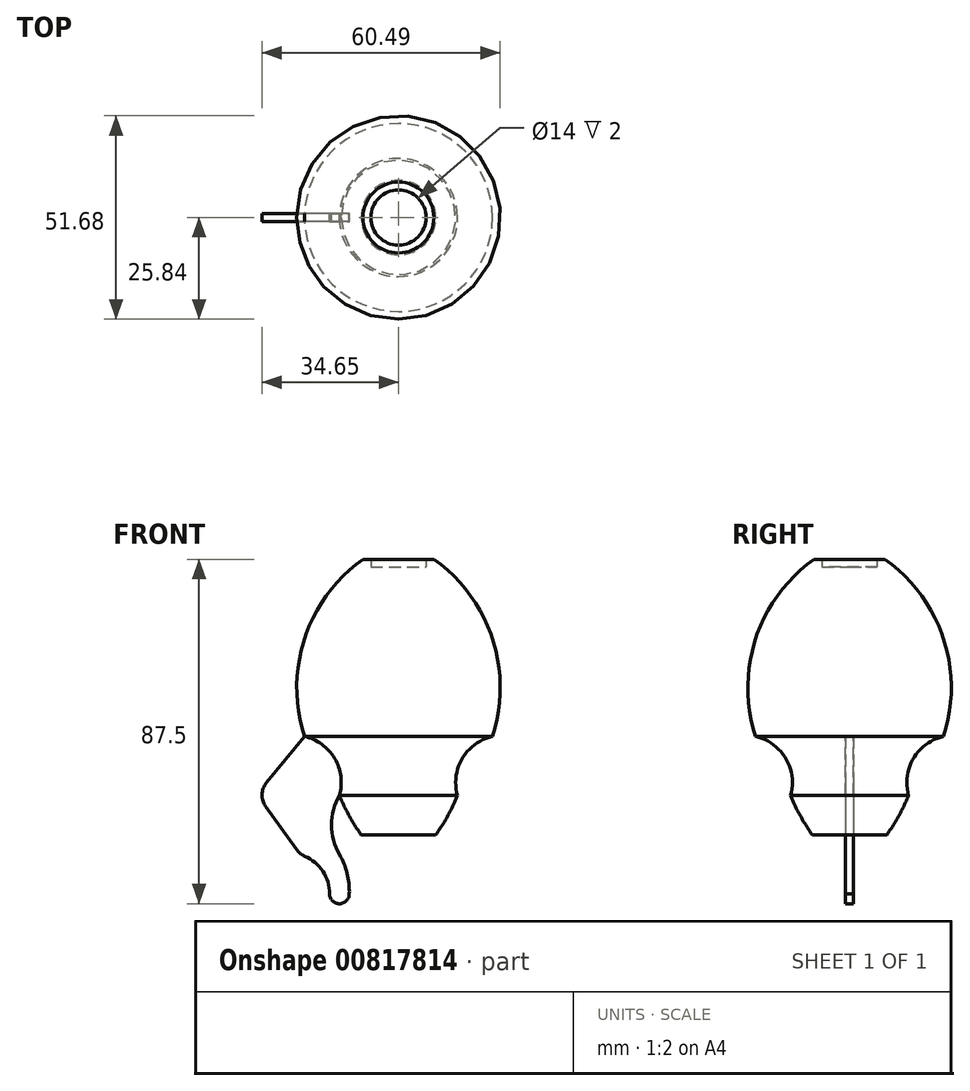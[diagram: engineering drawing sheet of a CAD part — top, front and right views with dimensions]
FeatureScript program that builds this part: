
annotation { "Feature Type Name" : "Feature", "Feature Type Description" : "" }
export const myFeature = defineFeature(function(context is Context, id is Id, definition is map)
    precondition{}
    {
        {
            var Q0;
            Q0=qCreatedBy(makeId("Front.planeOp"),FACE);
            var sketch = newSketch(context, id + "F0", { "sketchPlane" : qUnion([Q0])});
            skLineSegment(sketch, "E0", {"start": v(0, 0) * mm, "end": v(0, 80) * mm});
            skLineSegment(sketch, "E1", {"start": v(0, 20) * mm, "end": v(15, 20) * mm});
            skLineSegment(sketch, "E2", {"start": v(0, 35) * mm, "end": v(23.88, 35) * mm});
            skLineSegment(sketch, "E3", {"start": v(0, 80) * mm, "end": v(9, 80) * mm});
            skArc(sketch, "E4", {"start": v(23.88, 35) * mm, "mid": v(23.82, 59.94) * mm, "end": v(9, 80) * mm});
            skArc(sketch, "E5", {"start": v(23.88, 35) * mm, "mid": v(16.21, 29.41) * mm, "end": v(15, 20) * mm});
            skArc(sketch, "E6", {"start": v(0, 0) * mm, "mid": v(8.77, 9.05) * mm, "end": v(15, 20) * mm});
            skLineSegment(sketch, "E7", {"start": v(7, 80) * mm, "end": v(7, 78) * mm});
            skLineSegment(sketch, "E8", {"start": v(0, 78) * mm, "end": v(7, 78) * mm});
            skSolve(sketch);
        }
        {
            var Q0;
            {var subQ2=sQuery(id+"F0.wireOp",EDGE,"E1");Q0=makeQuery(id+"F0.imprint","IMPRINT",FACE,{"disambiguationData":[TD([[makeQuery(id+"F0.imprint","IMPRINT",EDGE,{"derivedFrom":subQ2}),-1.0]])]});}
            var Q1;
            {var subQ0=sQuery(id+"F0.wireOp",EDGE,"E1");Q1=makeQuery(id+"F0.imprint","IMPRINT",FACE,{"disambiguationData":[TD([[makeQuery(id+"F0.imprint","IMPRINT",EDGE,{"derivedFrom":subQ0}),1.0]])]});}
            var Q2;
            {var subQ1=sQuery(id+"F0.wireOp",EDGE,"E2");Q2=makeQuery(id+"F0.imprint","IMPRINT",FACE,{"disambiguationData":[TD([[makeQuery(id+"F0.imprint","IMPRINT",EDGE,{"derivedFrom":subQ1}),1.0]])]});}
            var Q3;
            Q3=sQuery(id+"F0.wireOp",EDGE,"E0");
            revolve(context, id + "F1", {"surfaceOperationType" : NewSurfaceOperationType.NEW, "entities" : qUnion([Q0, Q1, Q2]), "axis" : qUnion([Q3]), "revolveType" : RevolveType.FULL});
        }
        {
            var Q0;
            Q0=qCreatedBy(makeId("Front.planeOp"),FACE);
            var sketch = newSketch(context, id + "F2", { "sketchPlane" : qUnion([Q0])});
            skArc(sketch, "E9", {"start": v(-15, 20) * mm, "mid": v(-16.21, 29.41) * mm, "end": v(-23.88, 35) * mm});
            skArc(sketch, "E10", {"start": v(23.88, 35) * mm, "mid": v(16.21, 29.41) * mm, "end": v(15, 20) * mm});
            skLineSegment(sketch, "E11", {"start": v(0, 0) * mm, "end": v(0, -5) * mm});
            skLineSegment(sketch, "E12", {"start": v(0, -5) * mm, "end": v(-15, -5) * mm});
            skLineSegment(sketch, "E13", {"start": v(-15, -5) * mm, "end": v(-15, 5) * mm});
            skLineSegment(sketch, "E14", {"start": v(-25, 5) * mm, "end": v(-15, 5) * mm});
            skArc(sketch, "E15", {"start": v(-17.5, -5) * mm, "mid": v(-15, -7.5) * mm, "end": v(-12.5, -5) * mm});
            skLineSegment(sketch, "E16", {"start": v(-15, -5) * mm, "end": v(-17.5, -5) * mm});
            skArc(sketch, "E17", {"start": v(-15, 20) * mm, "mid": v(-17, 12.5) * mm, "end": v(-15, 5) * mm});
            skArc(sketch, "E18", {"start": v(-12.5, -5) * mm, "mid": v(-13.05, 0.18) * mm, "end": v(-15, 5) * mm});
            skLineSegment(sketch, "E19", {"start": v(-15, 20) * mm, "end": v(-23.88, 35) * mm});
            skArc(sketch, "E20", {"start": v(-17.5, -5) * mm, "mid": v(-19.22, 0.73) * mm, "end": v(-23.8, 4.57) * mm});
            skLineSegment(sketch, "E21", {"start": v(-23.88, 35) * mm, "end": v(-33.52, 23.25) * mm});
            skLineSegment(sketch, "E22", {"start": v(-33.72, 17.17) * mm, "end": v(-25.9, 6.25) * mm});
            skPoint(sketch, "E23.visualSharp", {"position": v(-35.95, 20.29) * mm});
            skArc(sketch, "E23.filletArc", {"start": v(-33.52, 23.25) * mm, "mid": v(-34.65, 20.25) * mm, "end": v(-33.72, 17.17) * mm});
            skPoint(sketch, "E24.visualSharp", {"position": v(-25, 5) * mm});
            skArc(sketch, "E24.filletArc", {"start": v(-25.9, 6.25) * mm, "mid": v(-24.97, 5.27) * mm, "end": v(-23.8, 4.57) * mm});
            skSolve(sketch);
        }
        {
            var Q0;
            Q0 = qSketchRegion(id + "F2", true);
            extrude(context, id + "F3", {"entities" : qUnion([Q0]), "operationType" : NewBodyOperationType.ADD, "endBound" : BoundingType.SYMMETRIC, "depth" : 2 * mm, "offsetDistance" : 25 * mm});
        }
        {
            var Q0;
            Q0=qCreatedBy(makeId("Top.planeOp"),FACE);
            var sketch = newSketch(context, id + "F4", { "sketchPlane" : qUnion([Q0])});
            skCircle(sketch, "E25", {"center": v(0, 0) * mm, "radius": 10 * mm});
            skSolve(sketch);
        }
        {
            var Q0;
            Q0=makeQuery(id+"F4.imprint","IMPRINT",FACE,{"disambiguationData":[TD([[makeQuery(id+"F4.imprint","IMPRINT",EDGE,{"derivedFrom":sQuery(id+"F4.wireOp",EDGE,"E25")}),1.0]])]});
            extrude(context, id + "F5", {"entities" : qUnion([Q0]), "operationType" : NewBodyOperationType.REMOVE, "depth" : 10 * mm, "offsetDistance" : 25 * mm});
        }
    });
